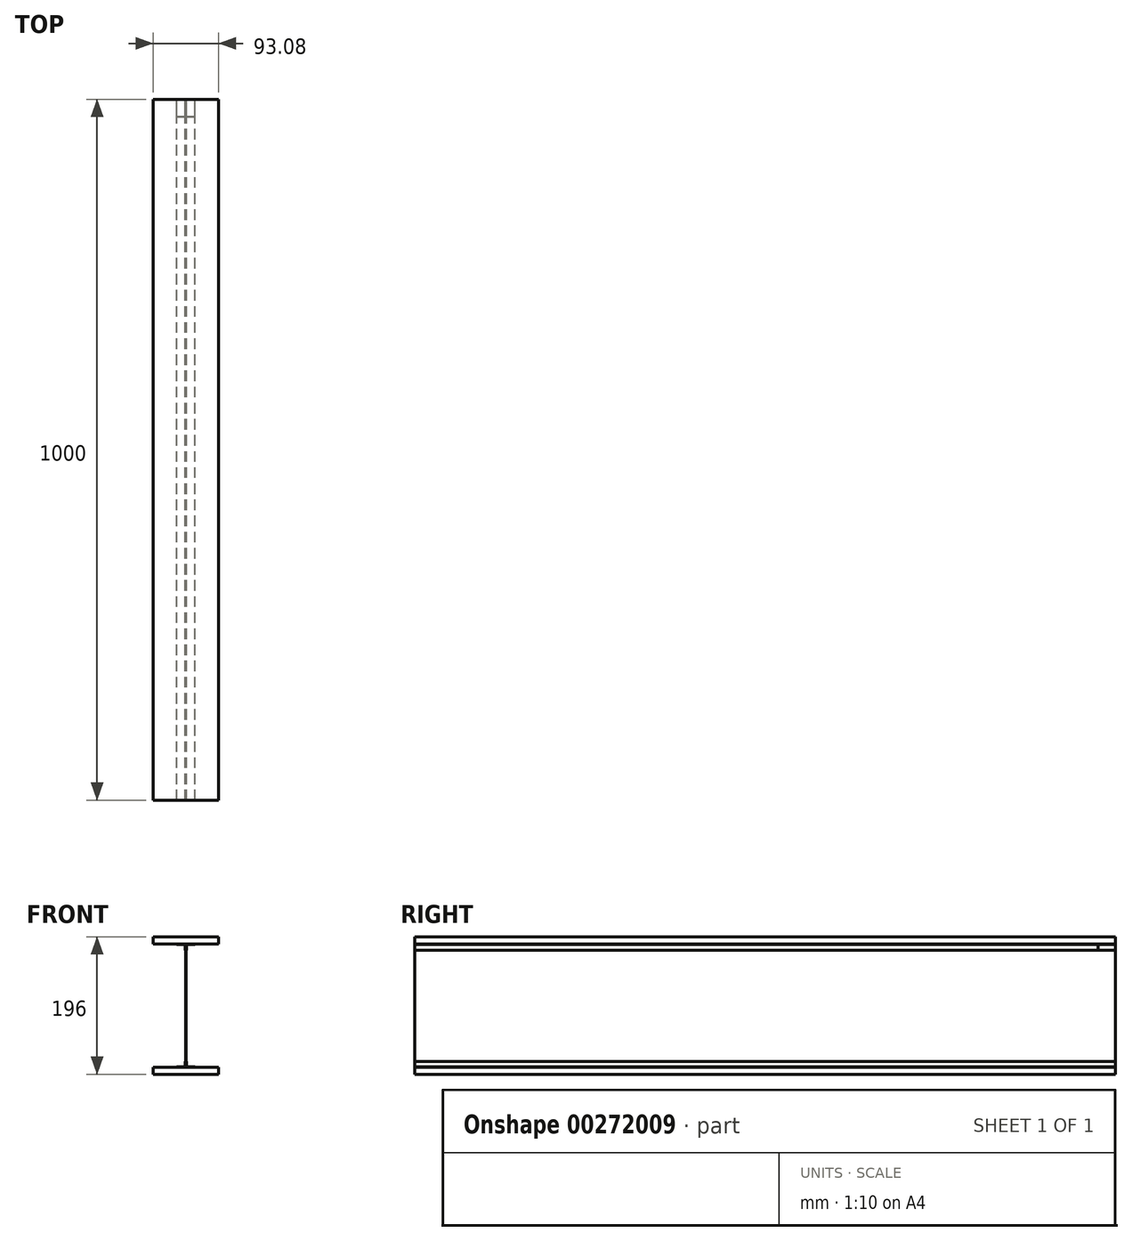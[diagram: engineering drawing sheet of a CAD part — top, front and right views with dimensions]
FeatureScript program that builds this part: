
annotation { "Feature Type Name" : "Feature", "Feature Type Description" : "" }
export const myFeature = defineFeature(function(context is Context, id is Id, definition is map)
    precondition{}
    {
        {
            var Q0;
            Q0=qCreatedBy(makeId("Front.planeOp"),FACE);
            var sketch = newSketch(context, id + "F0", { "sketchPlane" : qUnion([Q0])});
            skLineSegment(sketch, "E0.bottom", {"start": v(-46.54, 48.48) * mm, "end": v(46.54, 48.48) * mm});
            skLineSegment(sketch, "E0.top", {"start": v(-46.54, 38.48) * mm, "end": v(46.54, 38.48) * mm});
            skLineSegment(sketch, "E0.left", {"start": v(-46.54, 48.48) * mm, "end": v(-46.54, 38.48) * mm});
            skLineSegment(sketch, "E0.right", {"start": v(46.54, 48.48) * mm, "end": v(46.54, 38.48) * mm});
            skSolve(sketch);
        }
        {
            var Q0;
            Q0=qCreatedBy(makeId("Front.planeOp"),FACE);
            var sketch = newSketch(context, id + "F1", { "sketchPlane" : qUnion([Q0])});
            skLineSegment(sketch, "E1.top", {"start": v(-0.25, -137.52) * mm, "end": v(0.25, -137.52) * mm});
            skLineSegment(sketch, "E1.left", {"start": v(-0.25, 38.48) * mm, "end": v(-0.25, -137.52) * mm});
            skLineSegment(sketch, "E1.right", {"start": v(0.25, 38.48) * mm, "end": v(0.25, -137.52) * mm});
            skLineSegment(sketch, "E2", {"start": v(-0.25, 38.48) * mm, "end": v(0.25, 38.48) * mm});
            skSolve(sketch);
        }
        {
            var Q0;
            Q0=qCreatedBy(makeId("Front.planeOp"),FACE);
            var sketch = newSketch(context, id + "F2", { "sketchPlane" : qUnion([Q0])});
            skLineSegment(sketch, "E3.bottom", {"start": v(-46.54, -137.52) * mm, "end": v(46.54, -137.52) * mm});
            skLineSegment(sketch, "E3.top", {"start": v(-46.54, -147.52) * mm, "end": v(46.54, -147.52) * mm});
            skLineSegment(sketch, "E3.left", {"start": v(-46.54, -137.52) * mm, "end": v(-46.54, -147.52) * mm});
            skLineSegment(sketch, "E3.right", {"start": v(46.54, -137.52) * mm, "end": v(46.54, -147.52) * mm});
            skSolve(sketch);
        }
        {
            var Q0;
            Q0 = qSketchRegion(id + "F1", true);
            var Q1;
            Q1 = qSketchRegion(id + "F2", true);
            var Q2;
            Q2 = qSketchRegion(id + "F0", true);
            extrude(context, id + "F3", {"entities" : qUnion([Q0, Q1, Q2]), "depth" : 1000 * mm});
        }
        {
            var Q0;
            Q0=qCreatedBy(makeId("Front.planeOp"),FACE);
            var sketch = newSketch(context, id + "F4", { "sketchPlane" : qUnion([Q0])});
            skLineSegment(sketch, "E4", {"start": v(-13.1, -137.52) * mm, "end": v(-0.25, -137.52) * mm});
            skLineSegment(sketch, "E5", {"start": v(-0.25, -137.52) * mm, "end": v(-0.25, -129.52) * mm});
            skLineSegment(sketch, "E6", {"start": v(-0.25, -129.52) * mm, "end": v(-1.1, -129.52) * mm});
            skLineSegment(sketch, "E7", {"start": v(-1.1, -129.52) * mm, "end": v(-1.1, -136.67) * mm});
            skLineSegment(sketch, "E8", {"start": v(-1.1, -136.67) * mm, "end": v(-13.1, -136.67) * mm});
            skLineSegment(sketch, "E9", {"start": v(-13.1, -136.67) * mm, "end": v(-13.1, -137.52) * mm});
            skLineSegment(sketch, "E10", {"start": v(0.25, -129.52) * mm, "end": v(0.25, -137.52) * mm});
            skLineSegment(sketch, "E11", {"start": v(0.25, -137.52) * mm, "end": v(14.75, -137.52) * mm});
            skSolve(sketch);
        }
        {
            var Q0;
            Q0 = qSketchRegion(id + "F4", true);
            extrude(context, id + "F5", {"entities" : qUnion([Q0]), "depth" : 1000 * mm});
        }
        {
            var Q0;
            Q0=qCreatedBy(makeId("Front.planeOp"),FACE);
            var sketch = newSketch(context, id + "F6", { "sketchPlane" : qUnion([Q0])});
            skLineSegment(sketch, "E12", {"start": v(-13.1, 38.48) * mm, "end": v(-0.25, 38.48) * mm});
            skLineSegment(sketch, "E13", {"start": v(-0.25, 38.48) * mm, "end": v(-0.25, 29.63) * mm});
            skLineSegment(sketch, "E14", {"start": v(-0.25, 29.63) * mm, "end": v(-1.1, 29.63) * mm});
            skLineSegment(sketch, "E15", {"start": v(-1.1, 29.63) * mm, "end": v(-1.1, 37.63) * mm});
            skLineSegment(sketch, "E16", {"start": v(-1.1, 37.63) * mm, "end": v(-13.1, 37.63) * mm});
            skLineSegment(sketch, "E17", {"start": v(-13.1, 37.63) * mm, "end": v(-13.1, 38.48) * mm});
            skLineSegment(sketch, "E18", {"start": v(0.25, 29.63) * mm, "end": v(1.1, 29.63) * mm});
            skLineSegment(sketch, "E19", {"start": v(1.1, 29.63) * mm, "end": v(1.1, 37.63) * mm});
            skLineSegment(sketch, "E20", {"start": v(1.1, 37.63) * mm, "end": v(13.1, 37.63) * mm});
            skLineSegment(sketch, "E21", {"start": v(13.1, 37.63) * mm, "end": v(13.1, 38.48) * mm});
            skLineSegment(sketch, "E22", {"start": v(13.1, 38.48) * mm, "end": v(0.25, 38.48) * mm});
            skLineSegment(sketch, "E23", {"start": v(0.25, 38.48) * mm, "end": v(0.25, 29.63) * mm});
            skSolve(sketch);
        }
        {
            var Q0;
            Q0 = qSketchRegion(id + "F6", true);
            extrude(context, id + "F7", {"entities" : qUnion([Q0]), "depth" : 1000 * mm});
        }
        {
            var Q0;
            Q0 = qSketchRegion(id + "F6", true);
            extrude(context, id + "F8", {"entities" : qUnion([Q0]), "depth" : 25 * mm});
        }
        {
            var Q0;
            Q0=qCreatedBy(makeId("Front.planeOp"),FACE);
            var sketch = newSketch(context, id + "F9", { "sketchPlane" : qUnion([Q0])});
            skLineSegment(sketch, "E24", {"start": v(0.25, -129.52) * mm, "end": v(1.1, -129.52) * mm});
            skLineSegment(sketch, "E25", {"start": v(1.1, -129.52) * mm, "end": v(1.1, -136.67) * mm});
            skLineSegment(sketch, "E26", {"start": v(1.1, -136.67) * mm, "end": v(13.1, -136.67) * mm});
            skLineSegment(sketch, "E27", {"start": v(13.1, -136.67) * mm, "end": v(13.1, -137.52) * mm});
            skLineSegment(sketch, "E28", {"start": v(13.1, -137.52) * mm, "end": v(0.25, -137.52) * mm});
            skLineSegment(sketch, "E29", {"start": v(0.25, -137.52) * mm, "end": v(0.25, -129.52) * mm});
            skSolve(sketch);
        }
        {
            var Q0;
            Q0 = qSketchRegion(id + "F9", true);
            extrude(context, id + "F10", {"entities" : qUnion([Q0]), "depth" : 1000 * mm});
        }
    });
